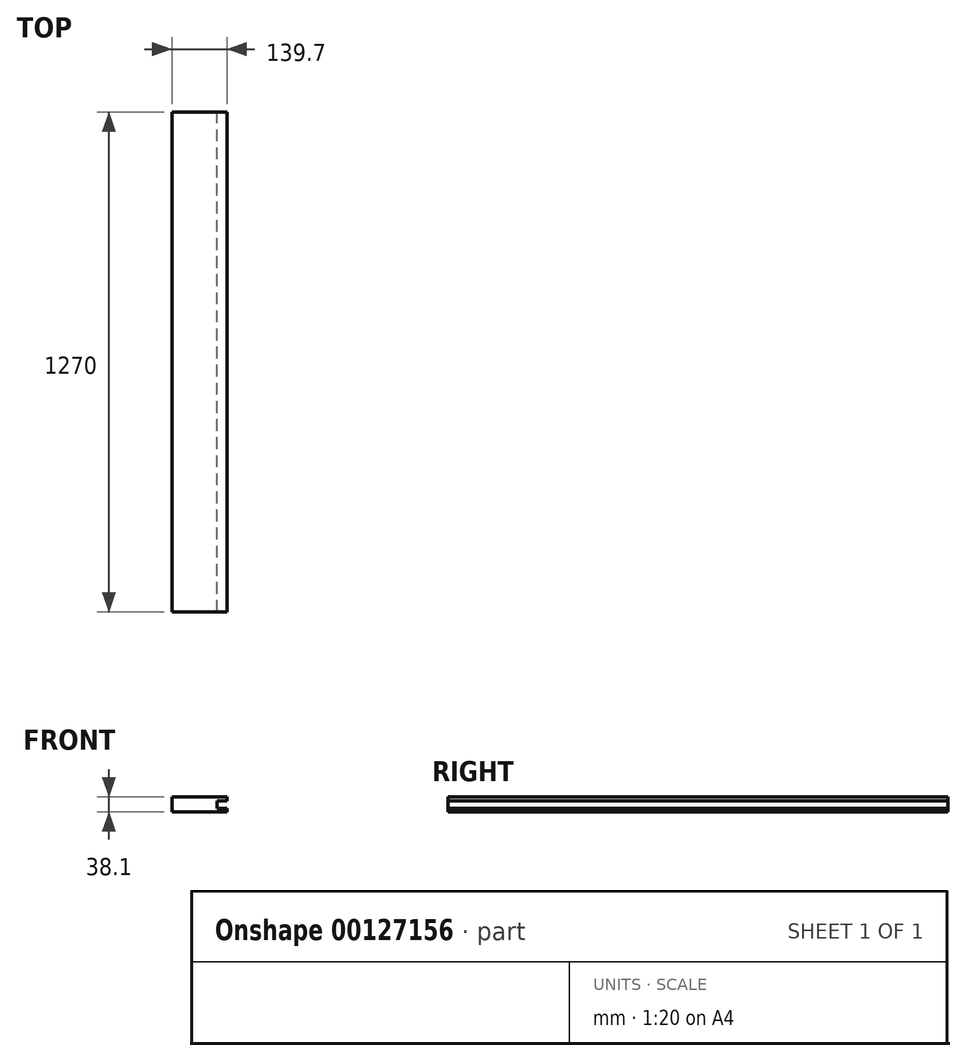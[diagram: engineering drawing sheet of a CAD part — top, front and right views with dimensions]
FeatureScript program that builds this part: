
annotation { "Feature Type Name" : "Feature", "Feature Type Description" : "" }
export const myFeature = defineFeature(function(context is Context, id is Id, definition is map)
    precondition{}
    {
        {
            var Q0;
            Q0=qCreatedBy(makeId("Front.planeOp"),FACE);
            var sketch = newSketch(context, id + "F0", { "sketchPlane" : qUnion([Q0])});
            skLineSegment(sketch, "E0.bottom", {"start": v(69.85, -19.05) * mm, "end": v(-69.85, -19.05) * mm});
            skLineSegment(sketch, "E0.top", {"start": v(69.85, 19.05) * mm, "end": v(-69.85, 19.05) * mm});
            skLineSegment(sketch, "E0.right", {"start": v(-69.85, -19.05) * mm, "end": v(-69.85, 19.05) * mm});
            skPoint(sketch, "E0.middle", {"position": v(0, 0) * mm});
            skLineSegment(sketch, "E1.top", {"start": v(69.85, 9.53) * mm, "end": v(44.45, 9.52) * mm});
            skLineSegment(sketch, "E1.right", {"start": v(44.45, 0) * mm, "end": v(44.45, 9.53) * mm});
            skLineSegment(sketch, "E2.top", {"start": v(69.85, -9.52) * mm, "end": v(44.45, -9.52) * mm});
            skLineSegment(sketch, "E2.right", {"start": v(44.45, 0) * mm, "end": v(44.45, -9.53) * mm});
            skLineSegment(sketch, "E3", {"start": v(69.85, 19.05) * mm, "end": v(69.85, 9.53) * mm});
            skLineSegment(sketch, "E4", {"start": v(69.85, -9.52) * mm, "end": v(69.85, -19.05) * mm});
            skSolve(sketch);
        }
        {
            var Q0;
            Q0=qSketchRegion(id+"F0",true);
            extrude(context, id + "F1", {"entities" : qUnion([Q0]), "depth" : 1270 * mm, "offsetDistance" : 25.4 * mm});
        }
    });
